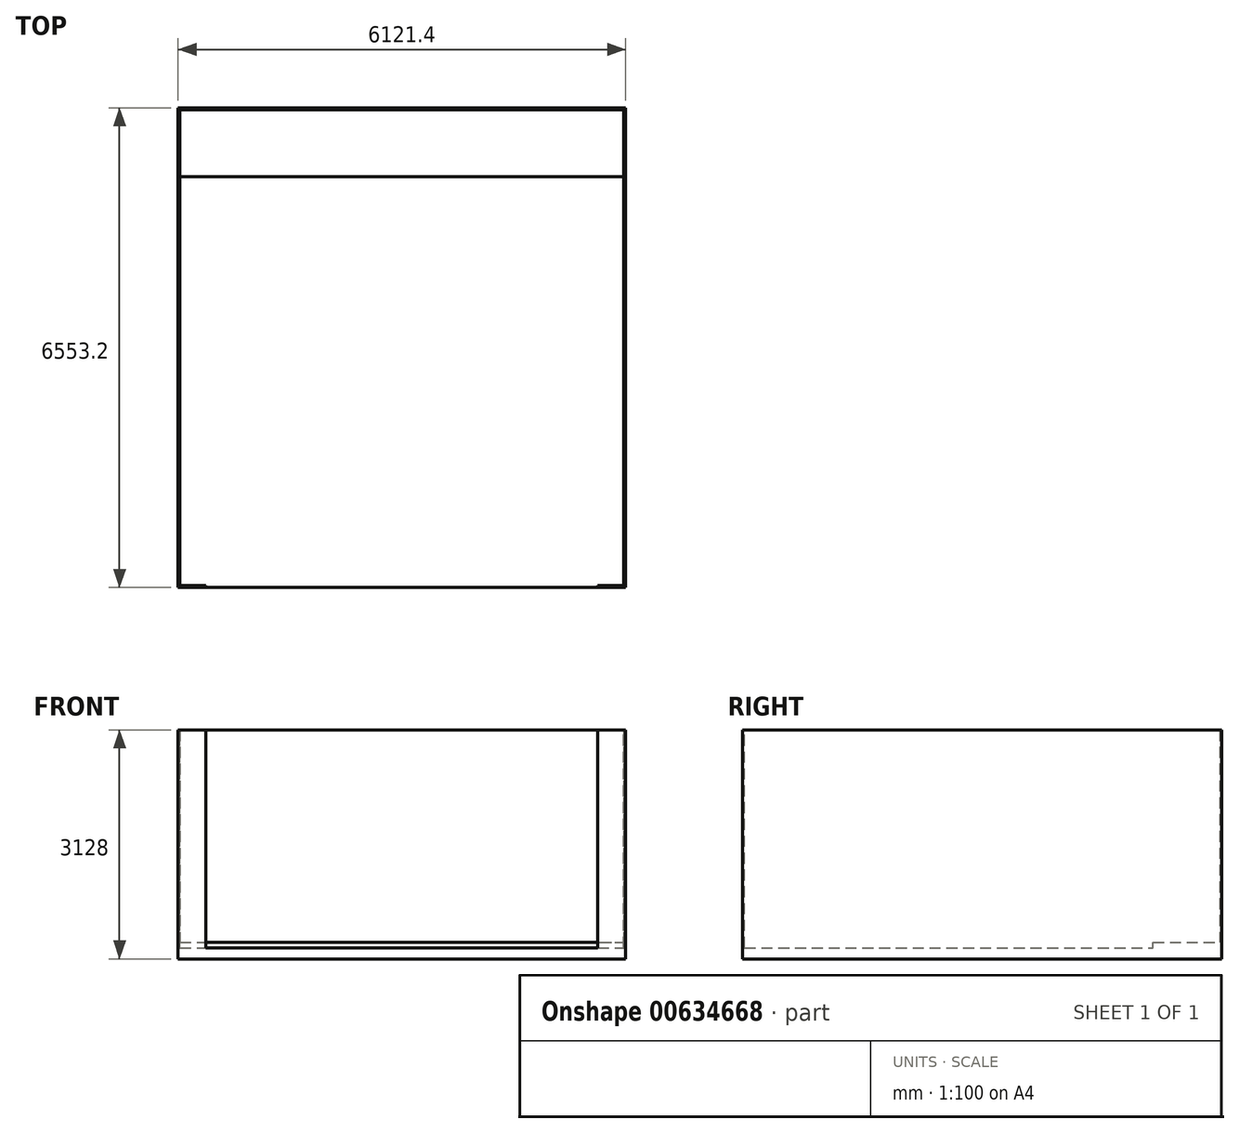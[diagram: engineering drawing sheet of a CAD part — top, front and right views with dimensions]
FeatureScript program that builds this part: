
annotation { "Feature Type Name" : "Feature", "Feature Type Description" : "" }
export const myFeature = defineFeature(function(context is Context, id is Id, definition is map)
    precondition{}
    {
        {
            var Q0;
            Q0=qCreatedBy(makeId("Top.planeOp"),FACE);
            var sketch = newSketch(context, id + "F0", { "sketchPlane" : qUnion([Q0])});
            skLineSegment(sketch, "E0.bottom", {"start": v(-3060.7, -6553.2) * mm, "end": v(3060.7, -6553.2) * mm});
            skLineSegment(sketch, "E0.top", {"start": v(-3060.7, 0) * mm, "end": v(3060.7, 0) * mm});
            skLineSegment(sketch, "E0.left", {"start": v(-3060.7, -6553.2) * mm, "end": v(-3060.7, 0) * mm});
            skLineSegment(sketch, "E0.right", {"start": v(3060.7, -6553.2) * mm, "end": v(3060.7, 0) * mm});
            skSolve(sketch);
        }
        {
            var Q0;
            Q0 = qSketchRegion(id + "F0", true);
            extrude(context, id + "F1", {"entities" : qUnion([Q0]), "depth" : 3048 * mm, "offsetDistance" : 25 * mm});
        }
        {
            var Q0;
            Q0=makeQuery(id+"F1.opExtrude","CAP_FACE",FACE,{"disambiguationData":[OSD([sQuery(id+"F0.wireOp",EDGE,"E0.bottom"),sQuery(id+"F0.wireOp",EDGE,"E0.top"),sQuery(id+"F0.wireOp",EDGE,"E0.left"),sQuery(id+"F0.wireOp",EDGE,"E0.right")])],"isStart":false});
            var sketch = newSketch(context, id + "F2", { "sketchPlane" : qUnion([Q0])});
            skLineSegment(sketch, "E1.bottom", {"start": v(-3035.3, -6553.2) * mm, "end": v(3035.3, -6553.2) * mm});
            skLineSegment(sketch, "E1.top", {"start": v(-3035.3, -939.8) * mm, "end": v(3035.3, -939.8) * mm});
            skLineSegment(sketch, "E1.left", {"start": v(-3035.3, -6553.2) * mm, "end": v(-3035.3, -939.8) * mm});
            skLineSegment(sketch, "E1.right", {"start": v(3035.3, -6553.2) * mm, "end": v(3035.3, -939.8) * mm});
            skSolve(sketch);
        }
        {
            var Q0;
            Q0 = qSketchRegion(id + "F2", true);
            extrude(context, id + "F3", {"entities" : qUnion([Q0]), "operationType" : NewBodyOperationType.REMOVE, "oppositeDirection" : true, "depth" : 2895.6 * mm, "offsetDistance" : 25 * mm});
        }
        {
            var Q0;
            Q0=makeQuery(id+"F1.opExtrude","CAP_FACE",FACE,{"disambiguationData":[OSD([sQuery(id+"F0.wireOp",EDGE,"E0.bottom"),sQuery(id+"F0.wireOp",EDGE,"E0.top"),sQuery(id+"F0.wireOp",EDGE,"E0.left"),sQuery(id+"F0.wireOp",EDGE,"E0.right")])],"isStart":false});
            var sketch = newSketch(context, id + "F4", { "sketchPlane" : qUnion([Q0])});
            skLineSegment(sketch, "E2.bottom", {"start": v(-3060.7, -6553.2) * mm, "end": v(-3035.3, -6553.2) * mm});
            skLineSegment(sketch, "E2.top", {"start": v(-3060.7, 0) * mm, "end": v(-3035.3, 0) * mm});
            skLineSegment(sketch, "E2.left", {"start": v(-3060.7, -6553.2) * mm, "end": v(-3060.7, 0) * mm});
            skLineSegment(sketch, "E2.right", {"start": v(-3035.3, -6553.2) * mm, "end": v(-3035.3, 0) * mm});
            skLineSegment(sketch, "E3.bottom", {"start": v(3035.3, -6553.2) * mm, "end": v(3060.7, -6553.2) * mm});
            skLineSegment(sketch, "E3.top", {"start": v(3035.3, 0) * mm, "end": v(3060.7, 0) * mm});
            skLineSegment(sketch, "E3.left", {"start": v(3035.3, -6553.2) * mm, "end": v(3035.3, 0) * mm});
            skLineSegment(sketch, "E3.right", {"start": v(3060.7, -6553.2) * mm, "end": v(3060.7, 0) * mm});
            skLineSegment(sketch, "E4.bottom", {"start": v(-3035.3, 0) * mm, "end": v(3035.3, 0) * mm});
            skLineSegment(sketch, "E4.top", {"start": v(-3035.3, -25.4) * mm, "end": v(3035.3, -25.4) * mm});
            skLineSegment(sketch, "E4.left", {"start": v(-3035.3, 0) * mm, "end": v(-3035.3, -25.4) * mm});
            skLineSegment(sketch, "E4.right", {"start": v(3035.3, 0) * mm, "end": v(3035.3, -25.4) * mm});
            skSolve(sketch);
        }
        {
            var Q0;
            Q0 = qSketchRegion(id + "F4", true);
            extrude(context, id + "F5", {"entities" : qUnion([Q0]), "operationType" : NewBodyOperationType.ADD, "depth" : 80 * mm, "offsetDistance" : 25 * mm});
        }
        {
            var Q0;
            Q0=makeQuery(id+"F1.opExtrude","CAP_FACE",FACE,{"disambiguationData":[OSD([sQuery(id+"F0.wireOp",EDGE,"E0.bottom"),sQuery(id+"F0.wireOp",EDGE,"E0.top"),sQuery(id+"F0.wireOp",EDGE,"E0.left"),sQuery(id+"F0.wireOp",EDGE,"E0.right")])],"isStart":false});
            extrude(context, id + "F6", {"entities" : qUnion([Q0]), "operationType" : NewBodyOperationType.REMOVE, "oppositeDirection" : true, "depth" : 2819.4 * mm, "offsetDistance" : 25.4 * mm});
        }
        {
            var Q0;
            {var subQ0=sQuery(id+"F4.wireOp",EDGE,"E2.right");Q0=makeQuery(id+"F6.boolean.opBoolean","MERGE",FACE,{"derivedFrom":[makeQuery(id+"F5.boolean.opBoolean","MERGE",FACE,{"derivedFrom":[makeQuery(id+"F3.boolean.opBoolean","COPY",FACE,{"derivedFrom":makeQuery(id+"F3.opExtrude","SWEPT_FACE",FACE,{"disambiguationData":[OSD([sQuery(id+"F2.wireOp",EDGE,"E1.left")])]})}),makeQuery(id+"F5.opExtrude","SWEPT_FACE",FACE,{"disambiguationData":[OSD([subQ0])]})]}),makeQuery(id+"F6.opExtrude","SWEPT_FACE",FACE,{"disambiguationData":[OSD([subQ0])]})]});}
            var sketch = newSketch(context, id + "F7", { "sketchPlane" : qUnion([Q0])});
            skLineSegment(sketch, "E5.bottom", {"start": v(-6553.2, 152.4) * mm, "end": v(-6527.8, 152.4) * mm});
            skLineSegment(sketch, "E5.top", {"start": v(-6553.2, 3128) * mm, "end": v(-6527.8, 3128) * mm});
            skLineSegment(sketch, "E5.left", {"start": v(-6553.2, 152.4) * mm, "end": v(-6553.2, 3128) * mm});
            skLineSegment(sketch, "E5.right", {"start": v(-6527.8, 152.4) * mm, "end": v(-6527.8, 3128) * mm});
            skSolve(sketch);
        }
        {
            var Q0;
            Q0 = qSketchRegion(id + "F7", true);
            extrude(context, id + "F8", {"entities" : qUnion([Q0]), "operationType" : NewBodyOperationType.ADD, "depth" : 355.6 * mm, "offsetDistance" : 25.4 * mm});
        }
        {
            var Q0;
            {var subQ0=sQuery(id+"F4.wireOp",EDGE,"E3.left");Q0=makeQuery(id+"F6.boolean.opBoolean","MERGE",FACE,{"derivedFrom":[makeQuery(id+"F5.boolean.opBoolean","MERGE",FACE,{"derivedFrom":[makeQuery(id+"F3.boolean.opBoolean","COPY",FACE,{"derivedFrom":makeQuery(id+"F3.opExtrude","SWEPT_FACE",FACE,{"disambiguationData":[OSD([sQuery(id+"F2.wireOp",EDGE,"E1.right")])]})}),makeQuery(id+"F5.opExtrude","SWEPT_FACE",FACE,{"disambiguationData":[OSD([subQ0])]})]}),makeQuery(id+"F6.opExtrude","SWEPT_FACE",FACE,{"disambiguationData":[OSD([subQ0])]})]});}
            var sketch = newSketch(context, id + "F9", { "sketchPlane" : qUnion([Q0])});
            skLineSegment(sketch, "E6.bottom", {"start": v(6553.2, 152.4) * mm, "end": v(6527.8, 152.4) * mm});
            skLineSegment(sketch, "E6.top", {"start": v(6553.2, 3128) * mm, "end": v(6527.8, 3128) * mm});
            skLineSegment(sketch, "E6.left", {"start": v(6553.2, 152.4) * mm, "end": v(6553.2, 3128) * mm});
            skLineSegment(sketch, "E6.right", {"start": v(6527.8, 152.4) * mm, "end": v(6527.8, 3128) * mm});
            skSolve(sketch);
        }
        {
            var Q0;
            Q0 = qSketchRegion(id + "F9", true);
            extrude(context, id + "F10", {"entities" : qUnion([Q0]), "operationType" : NewBodyOperationType.ADD, "depth" : 355.6 * mm, "offsetDistance" : 25.4 * mm});
        }
    });
